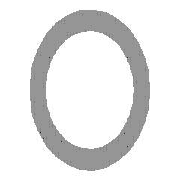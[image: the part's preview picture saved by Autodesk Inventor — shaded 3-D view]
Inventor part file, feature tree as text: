
AUTODESK INVENTOR PART (.ipt)
format: ipt  version: 2021 (Build 250183000, 183)  size: 342,528 bytes
history: native  units: mm (DEFAULTED — no unit token found)
features: other x5, plane x2, sketch x2, sweep x1
ambient origin geometry x8: Origin, YZ Plane, XZ Plane, XY Plane, X Axis, Y Axis, Z Axis, Center Point
bodies: Solid1 (feature_tree)
feature tree (10):
  parser-record x1  (decoder bookkeeping rows leaked as tree rows — omitted from the tree; the rows remain in map.json)
  other  "Driven Length"
  other  "Plano inicial"
  other  "Plano final"
  other  "Trayectoria de barrido"
  plane  "Plano de trabajo de orientación"
  sweep  "Cuerpo"
  sketch  "Sketch3"  dims[d0=21.336mm d1=3.7338mm]
  plane  "Work Plane3"
  sketch  "Sketch4"  dims[d4=-0.0mm d5=1183.592627mm d6=90.0deg d7=1183.592627mm d8=0.0mm d9=0.0mm]
